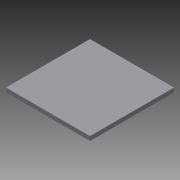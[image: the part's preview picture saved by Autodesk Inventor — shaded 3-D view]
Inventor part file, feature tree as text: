
AUTODESK INVENTOR PART (.ipt)
format: ipt  version: 2013 (Build 170138000, 138)  size: 64,512 bytes
history: native  units: mm
features: extrude x1, sketch x1
ambient origin geometry x8: Origin, YZ Plane, XZ Plane, XY Plane, X Axis, Y Axis, Z Axis, Center Point
bodies: Solid1 (feature_tree)
feature tree (2):
  extrude  "Extrusion1"  Depth=10.0mm TaperAngle=0.0deg
  sketch  "Sketch1"  dims[d0=200.0mm d2=10.0mm d3=0.0mm]
